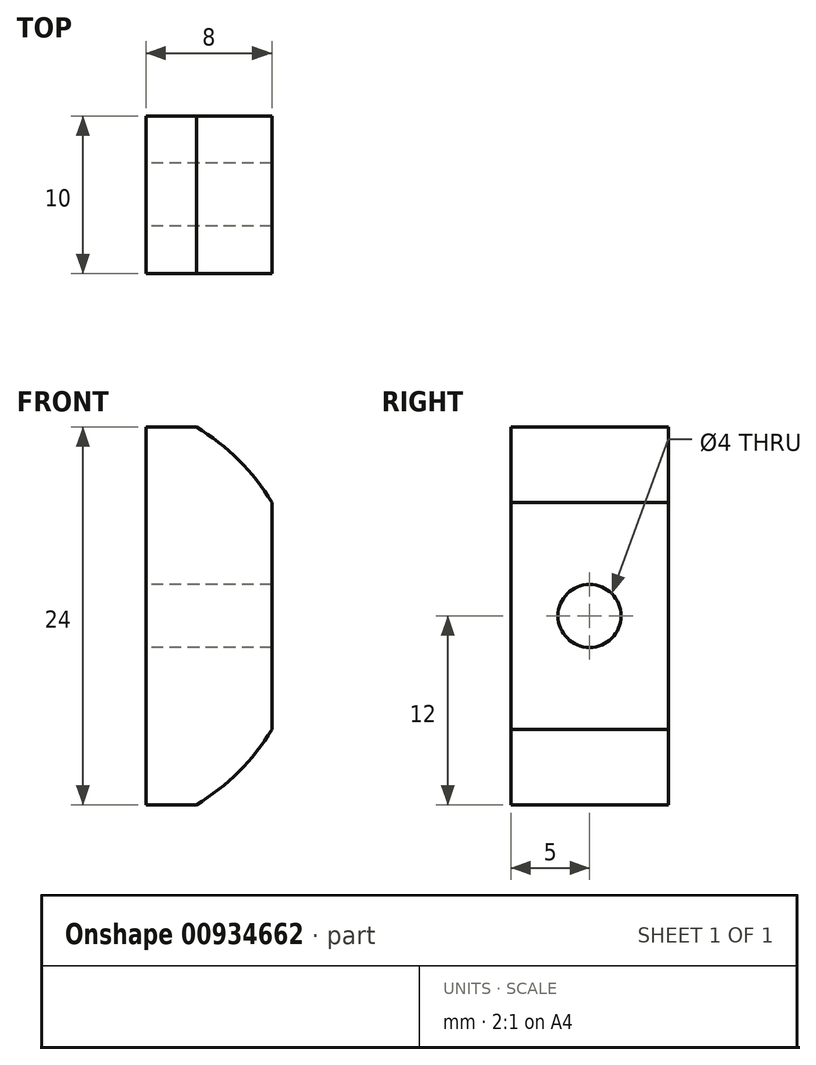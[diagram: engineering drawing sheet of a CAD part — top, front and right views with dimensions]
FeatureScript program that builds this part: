
annotation { "Feature Type Name" : "Feature", "Feature Type Description" : "" }
export const myFeature = defineFeature(function(context is Context, id is Id, definition is map)
    precondition{}
    {
        {
            var Q0;
            Q0=qCreatedBy(makeId("Front.planeOp"),FACE);
            var sketch = newSketch(context, id + "F0", { "sketchPlane" : qUnion([Q0])});
            skLineSegment(sketch, "E0", {"start": v(4, 12) * mm, "end": v(4, -12) * mm});
            skLineSegment(sketch, "E1", {"start": v(4, -12) * mm, "end": v(7.21, -12) * mm});
            skLineSegment(sketch, "E2", {"start": v(4, 12) * mm, "end": v(7.21, 12) * mm});
            skLineSegment(sketch, "E3", {"start": v(12, 7.21) * mm, "end": v(12, -7.21) * mm});
            skArc(sketch, "E4", {"start": v(7.21, -12) * mm, "mid": v(9.9, -9.9) * mm, "end": v(12, -7.21) * mm});
            skPoint(sketch, "E5.orphan", {"position": v(12, -12) * mm});
            skPoint(sketch, "E6.orphan", {"position": v(12, 12) * mm});
            skArc(sketch, "E7.trimOffspring", {"start": v(12, 7.21) * mm, "mid": v(9.9, 9.9) * mm, "end": v(7.21, 12) * mm});
            skSolve(sketch);
        }
        {
            var Q0;
            Q0 = qSketchRegion(id + "F0", true);
            extrude(context, id + "F1", {"entities" : qUnion([Q0]), "oppositeDirection" : true, "depth" : 10 * mm, "offsetDistance" : 25 * mm});
        }
        {
            var Q0;
            Q0=makeQuery(id+"F1.opExtrude","SWEPT_FACE",FACE,{"disambiguationData":[OSD([sQuery(id+"F0.wireOp",EDGE,"E0")])]});
            var sketch = newSketch(context, id + "F2", { "sketchPlane" : qUnion([Q0])});
            skCircle(sketch, "E8", {"center": v(-5, 0) * mm, "radius": 2 * mm});
            skSolve(sketch);
        }
        {
            var Q0;
            Q0 = qSketchRegion(id + "F2", true);
            extrude(context, id + "F3", {"entities" : qUnion([Q0]), "operationType" : NewBodyOperationType.REMOVE, "oppositeDirection" : true, "depth" : 25 * mm, "offsetDistance" : 25 * mm});
        }
    });
